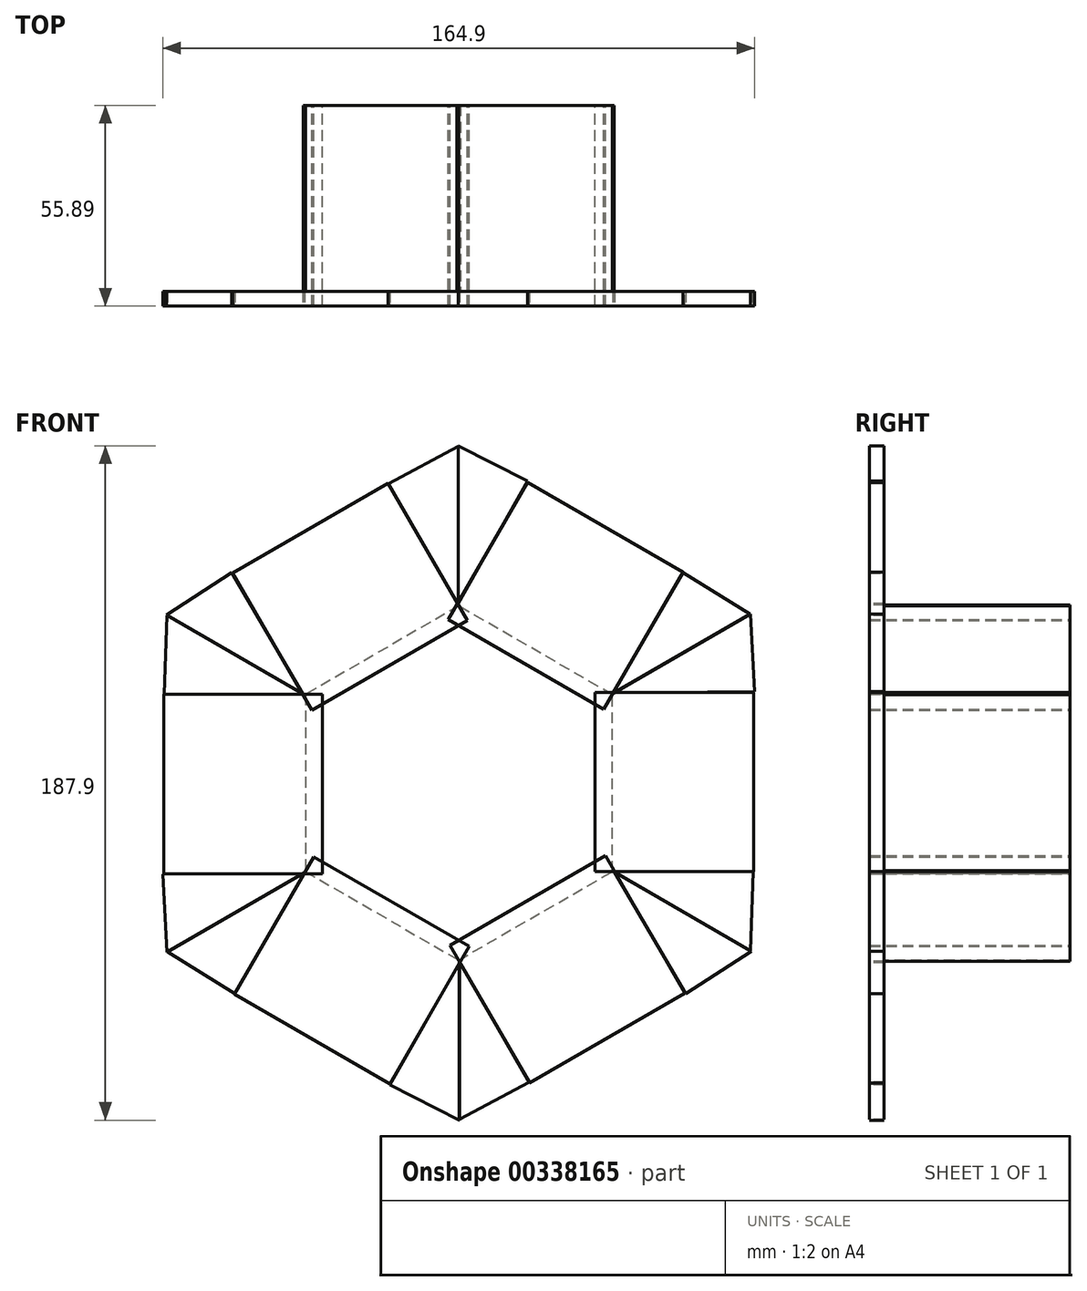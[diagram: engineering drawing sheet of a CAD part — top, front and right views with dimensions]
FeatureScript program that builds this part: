
annotation { "Feature Type Name" : "Feature", "Feature Type Description" : "" }
export const myFeature = defineFeature(function(context is Context, id is Id, definition is map)
    precondition{}
    {
        {
            var Q0;
            Q0=qCreatedBy(makeId("Top.planeOp"),FACE);
            var sketch = newSketch(context, id + "F0", { "sketchPlane" : qUnion([Q0])});
            skLineSegment(sketch, "E0", {"start": v(0, 0) * mm, "end": v(0, 55.9) * mm});
            skLineSegment(sketch, "E1", {"start": v(4.74, 55.9) * mm, "end": v(4.74, 6.31) * mm});
            skLineSegment(sketch, "E2", {"start": v(44.18, 0) * mm, "end": v(0, 0) * mm});
            skLineSegment(sketch, "E3", {"start": v(4.74, 55.9) * mm, "end": v(0, 55.9) * mm});
            skLineSegment(sketch, "E4", {"start": v(44.18, 0) * mm, "end": v(44.18, 4.06) * mm});
            skLineSegment(sketch, "E5", {"start": v(44.18, 4.06) * mm, "end": v(4.74, 4.06) * mm});
            skLineSegment(sketch, "E6", {"start": v(4.74, 6.31) * mm, "end": v(4.74, 4.06) * mm});
            skSolve(sketch);
        }
        {
            var Q0;
            Q0=makeQuery(id+"F0.imprint","IMPRINT",FACE,{"disambiguationData":[TD([[makeQuery(id+"F0.imprint","IMPRINT",EDGE,{"derivedFrom":sQuery(id+"F0.wireOp",EDGE,"E0")}),-1.0]])]});
            extrude(context, id + "F1", {"entities" : qUnion([Q0]), "oppositeDirection" : true, "depth" : 50 * mm});
        }
        {
            var Q0;
            Q0=qCreatedBy(makeId("Right.planeOp"),FACE);
            cPlane(context, id + "F2", {"entities" : qUnion([Q0]), "cplaneType" : CPlaneType.OFFSET, "offset" : 38 * mm, "oppositeDirection" : true, "width" : 152.4 * mm, "height" : 152.4 * mm});
        }
        {
            var Q0;
            Q0=qCreatedBy(id+"F2.planeOp",FACE);
            var sketch = newSketch(context, id + "F3", { "sketchPlane" : qUnion([Q0])});
            skLineSegment(sketch, "E7", {"start": v(-2.66, 0) * mm, "end": v(-2.66, -50.57) * mm});
            skLineSegment(sketch, "E8", {"start": v(-2.66, -50.57) * mm, "end": v(-2.66, -25.29) * mm});
            skLineSegment(sketch, "E9", {"start": v(-2.66, -25.29) * mm, "end": v(81.78, -25.29) * mm});
            skSolve(sketch);
        }
        {
            var Q0;
            Q0=makeQuery(id+"F1.opExtrude","SWEPT_BODY",BODY,{"disambiguationData":[OSD([sQuery(id+"F0.wireOp",EDGE,"E0"),sQuery(id+"F0.wireOp",EDGE,"E1"),sQuery(id+"F0.wireOp",EDGE,"E2"),sQuery(id+"F0.wireOp",EDGE,"E3"),sQuery(id+"F0.wireOp",EDGE,"E4"),sQuery(id+"F0.wireOp",EDGE,"E5"),sQuery(id+"F0.wireOp",EDGE,"E6")])]});
            var Q1;
            Q1=sQuery(id+"F3.wireOp",EDGE,"E9");
            circularPattern(context, id + "F4", {"entities" : qUnion([Q0]), "axis" : qUnion([Q1]), "angle" : 360 * degree, "instanceCount" : 6, "equalSpace" : true});
        }
        {
            var Q0;
            Q0=qCreatedBy(makeId("Front.planeOp"),FACE);
            var sketch = newSketch(context, id + "F5", { "sketchPlane" : qUnion([Q0])});
            skLineSegment(sketch, "E10", {"start": v(-57.62, 58.09) * mm, "end": v(-38.16, 68.5) * mm});
            skLineSegment(sketch, "E11", {"start": v(-38.16, 68.5) * mm, "end": v(-38.16, 24.38) * mm});
            skLineSegment(sketch, "E12", {"start": v(-38.16, 24.38) * mm, "end": v(-57.62, 58.09) * mm});
            skSolve(sketch);
        }
        {
            var Q0;
            Q0=makeQuery(id+"F5.imprint","IMPRINT",FACE,{"disambiguationData":[TD([[makeQuery(id+"F5.imprint","IMPRINT",EDGE,{"derivedFrom":sQuery(id+"F5.wireOp",EDGE,"E10")}),-1.0]])]});
            var Q1;
            Q1=makeQuery(id+"F4.opPattern","COPY",FACE,{"derivedFrom":makeQuery(id+"F1.opExtrude","SWEPT_FACE",FACE,{"disambiguationData":[OSD([sQuery(id+"F0.wireOp",EDGE,"E5")])]}),"instanceName":"4"});
            extrude(context, id + "F6", {"entities" : qUnion([Q0]), "endBound" : BoundingType.UP_TO_SURFACE, "oppositeDirection" : true, "endBoundEntityFace" : qUnion([Q1]), "depth" : 25.4 * mm});
        }
        {
            var Q0;
            Q0=makeQuery(id+"F6.opExtrude","SWEPT_BODY",BODY,{"disambiguationData":[OSD([sQuery(id+"F5.wireOp",EDGE,"E10"),sQuery(id+"F5.wireOp",EDGE,"E11"),sQuery(id+"F5.wireOp",EDGE,"E12")])]});
            var Q1;
            Q1=sQuery(id+"F3.wireOp",EDGE,"E9");
            circularPattern(context, id + "F7", {"entities" : qUnion([Q0]), "axis" : qUnion([Q1]), "angle" : 360 * degree, "instanceCount" : 6, "equalSpace" : true});
        }
        {
            var Q0;
            Q0=qCreatedBy(makeId("Front.planeOp"),FACE);
            var sketch = newSketch(context, id + "F8", { "sketchPlane" : qUnion([Q0])});
            skLineSegment(sketch, "E13", {"start": v(-18.81, 58.85) * mm, "end": v(-38.16, 68.66) * mm});
            skLineSegment(sketch, "E14", {"start": v(-38.16, 68.66) * mm, "end": v(-38.16, 24.77) * mm});
            skLineSegment(sketch, "E15", {"start": v(-18.81, 58.85) * mm, "end": v(-38.16, 24.77) * mm});
            skSolve(sketch);
        }
        {
            var Q0;
            Q0=makeQuery(id+"F8.imprint","IMPRINT",FACE,{"disambiguationData":[TD([[makeQuery(id+"F8.imprint","IMPRINT",EDGE,{"derivedFrom":sQuery(id+"F8.wireOp",EDGE,"E13")}),1.0]])]});
            var Q1;
            Q1=makeQuery(id+"F6.opExtrude","CAP_FACE",FACE,{"disambiguationData":[OSD([sQuery(id+"F5.wireOp",EDGE,"E10"),sQuery(id+"F5.wireOp",EDGE,"E11"),sQuery(id+"F5.wireOp",EDGE,"E12")])],"isStart":false});
            extrude(context, id + "F9", {"entities" : qUnion([Q0]), "endBound" : BoundingType.UP_TO_SURFACE, "oppositeDirection" : true, "endBoundEntityFace" : qUnion([Q1]), "depth" : 25.4 * mm});
        }
        {
            var Q0;
            Q0=makeQuery(id+"F9.opExtrude","SWEPT_BODY",BODY,{"disambiguationData":[OSD([sQuery(id+"F8.wireOp",EDGE,"E13"),sQuery(id+"F8.wireOp",EDGE,"E14"),sQuery(id+"F8.wireOp",EDGE,"E15")])]});
            var Q1;
            Q1=sQuery(id+"F3.wireOp",EDGE,"E9");
            circularPattern(context, id + "F10", {"entities" : qUnion([Q0]), "axis" : qUnion([Q1]), "angle" : 360 * degree, "instanceCount" : 6, "equalSpace" : true});
        }
    });
